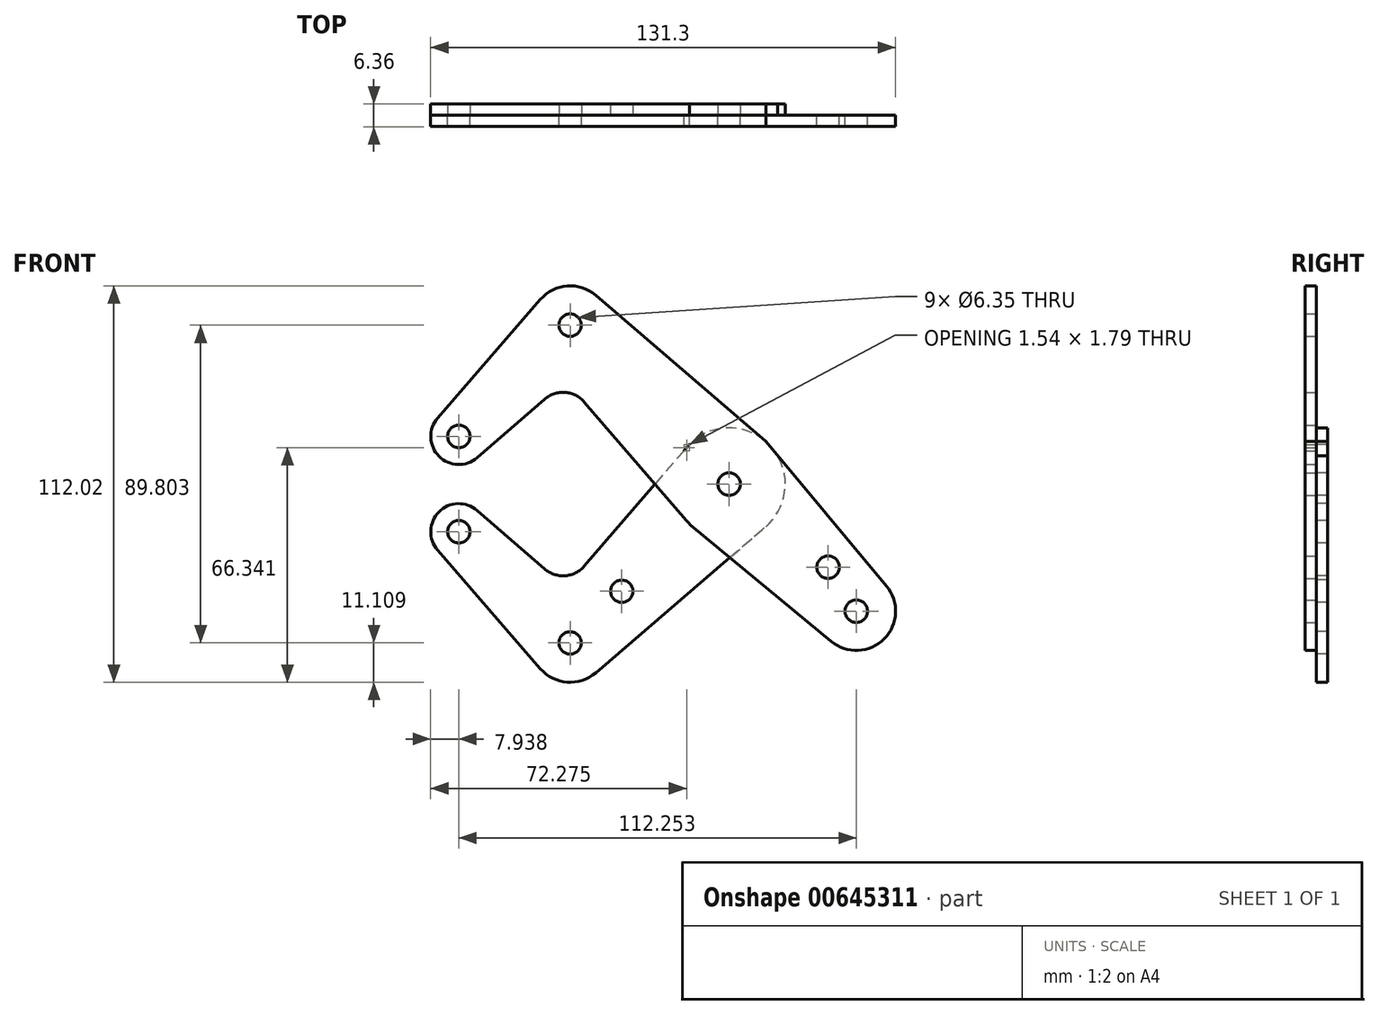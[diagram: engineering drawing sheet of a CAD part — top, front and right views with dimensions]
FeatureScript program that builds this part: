
annotation { "Feature Type Name" : "Feature", "Feature Type Description" : "" }
export const myFeature = defineFeature(function(context is Context, id is Id, definition is map)
    precondition{}
    {
        {
            var Q0;
            Q0=qCreatedBy(makeId("Front.planeOp"),FACE);
            var sketch = newSketch(context, id + "F0", { "sketchPlane" : qUnion([Q0])});
            skLineSegment(sketch, "E0", {"start": v(-76.33, 13.47) * mm, "end": v(-44.9, 44.9) * mm, "construction": true});
            skLineSegment(sketch, "E1", {"start": v(-44.9, 44.9) * mm, "end": v(35.92, -35.92) * mm, "construction": true});
            skCircle(sketch, "E2", {"center": v(-76.33, 13.47) * mm, "radius": 3.18 * mm});
            skCircle(sketch, "E3", {"center": v(-76.33, 13.47) * mm, "radius": 7.94 * mm});
            skCircle(sketch, "E4", {"center": v(-44.9, 44.9) * mm, "radius": 11.11 * mm});
            skCircle(sketch, "E5", {"center": v(-44.9, 44.9) * mm, "radius": 3.18 * mm});
            skCircle(sketch, "E6", {"center": v(0, 0) * mm, "radius": 15.88 * mm});
            skCircle(sketch, "E7", {"center": v(0, 0) * mm, "radius": 3.98 * mm});
            skCircle(sketch, "E8", {"center": v(0, 0) * mm, "radius": 3.18 * mm});
            skCircle(sketch, "E9", {"center": v(35.92, -35.92) * mm, "radius": 11.11 * mm});
            skCircle(sketch, "E10", {"center": v(35.92, -35.92) * mm, "radius": 3.18 * mm});
            skCircle(sketch, "E11", {"center": v(27.97, -23.48) * mm, "radius": 3.17 * mm});
            skLineSegment(sketch, "E12", {"start": v(-82.33, 18.67) * mm, "end": v(-53.3, 52.18) * mm});
            skLineSegment(sketch, "E13", {"start": v(-71.13, 7.47) * mm, "end": v(-52.08, 23.98) * mm});
            skLineSegment(sketch, "E14", {"start": v(-37.66, 53.33) * mm, "end": v(10.35, 12.04) * mm});
            skLineSegment(sketch, "E15", {"start": v(-10.12, -12.23) * mm, "end": v(28.83, -44.48) * mm});
            skLineSegment(sketch, "E16", {"start": v(10.35, 12.04) * mm, "end": v(44.45, -28.8) * mm});
            skArc(sketch, "E17.filletArc", {"start": v(-40.85, 23.15) * mm, "mid": v(-46.3, 25.9) * mm, "end": v(-52.08, 23.98) * mm});
            skLineSegment(sketch, "E18", {"start": v(0, 0) * mm, "end": v(-44.9, -44.9) * mm, "construction": true});
            skLineSegment(sketch, "E19", {"start": v(-44.9, -44.9) * mm, "end": v(-76.33, -13.47) * mm, "construction": true});
            skCircle(sketch, "E20", {"center": v(-76.33, -13.47) * mm, "radius": 7.94 * mm});
            skCircle(sketch, "E21", {"center": v(-76.33, -13.47) * mm, "radius": 3.18 * mm});
            skCircle(sketch, "E22", {"center": v(-44.9, -44.9) * mm, "radius": 11.11 * mm});
            skCircle(sketch, "E23", {"center": v(-44.9, -44.9) * mm, "radius": 3.18 * mm});
            skCircle(sketch, "E24", {"center": v(-30.3, -30.3) * mm, "radius": 3.18 * mm});
            skLineSegment(sketch, "E25", {"start": v(-11.23, 11.23) * mm, "end": v(-40.84, -23.16) * mm});
            skLineSegment(sketch, "E26", {"start": v(-37.66, -53.33) * mm, "end": v(11.26, -11.26) * mm});
            skLineSegment(sketch, "E27", {"start": v(-82.33, -18.67) * mm, "end": v(-53.3, -52.18) * mm});
            skLineSegment(sketch, "E28", {"start": v(-71.13, -7.47) * mm, "end": v(-52.07, -23.98) * mm});
            skArc(sketch, "E29.filletArc", {"start": v(-52.07, -23.98) * mm, "mid": v(-46.29, -25.9) * mm, "end": v(-40.84, -23.16) * mm});
            skLineSegment(sketch, "E30", {"start": v(-40.85, 23.15) * mm, "end": v(-12.04, -10.35) * mm});
            skSolve(sketch);
        }
        {
            var Q0;
            Q0=makeQuery(id+"F0.imprint","IMPRINT",FACE,{"disambiguationData":[TD([[makeQuery(id+"F0.imprint","IMPRINT",EDGE,{"derivedFrom":sQuery(id+"F0.wireOp",EDGE,"E2")}),-1.0]])]});
            var Q1;
            Q1=makeQuery(id+"F0.imprint","IMPRINT",FACE,{"disambiguationData":[TD([[makeQuery(id+"F0.imprint","IMPRINT",EDGE,{"derivedFrom":sQuery(id+"F0.wireOp",EDGE,"E5")}),-1.0]])]});
            var Q2;
            {var subQ5=sQuery(id+"F0.wireOp",EDGE,"E12");Q2=makeQuery(id+"F0.imprint","IMPRINT",FACE,{"disambiguationData":[TD([[makeQuery(id+"F0.imprint","IMPRINT",EDGE,{"derivedFrom":subQ5}),-1.0]])]});}
            var Q3;
            {var subQ0=sQuery(id+"F0.wireOp",EDGE,"MmRiEuoZ-qYsz-kD5B-3HoX-GEw2XtJWGpv0");var subQ3=sQuery(id+"F0.wireOp",EDGE,"E25");var subQ5=makeQuery(id+"F0.imprint","INTERSECT",VERTEX,{"derivedFrom":[subQ0,subQ3]});Q3=makeQuery(id+"F0.imprint","IMPRINT",FACE,{"disambiguationData":[TD([[makeQuery(id+"F0.imprint","IMPRINT",EDGE,{"disambiguationData":[TD([[subQ5,1.0]])],"derivedFrom":subQ3}),1.0]])]});}
            var Q4;
            Q4=makeQuery(id+"F0.imprint","IMPRINT",FACE,{"disambiguationData":[TD([[makeQuery(id+"F0.imprint","IMPRINT",EDGE,{"derivedFrom":sQuery(id+"F0.wireOp",EDGE,"E7")}),-1.0]])]});
            var Q5;
            Q5=makeQuery(id+"F0.imprint","IMPRINT",FACE,{"disambiguationData":[TD([[makeQuery(id+"F0.imprint","IMPRINT",EDGE,{"derivedFrom":sQuery(id+"F0.wireOp",EDGE,"E7")}),1.0]])]});
            var Q6;
            {var subQ1=sQuery(id+"F0.wireOp",EDGE,"E6");var subQ3=sQuery(id+"F0.wireOp",EDGE,"E26");var subQ4=makeQuery(id+"F0.imprint","INTERSECT",VERTEX,{"derivedFrom":[subQ1,subQ3]});Q6=makeQuery(id+"F0.imprint","IMPRINT",FACE,{"disambiguationData":[TD([[makeQuery(id+"F0.imprint","IMPRINT",EDGE,{"disambiguationData":[TD([[subQ4,1.0]])],"derivedFrom":subQ3}),1.0]])]});}
            var Q7;
            Q7=makeQuery(id+"F0.imprint","IMPRINT",FACE,{"disambiguationData":[TD([[makeQuery(id+"F0.imprint","IMPRINT",EDGE,{"derivedFrom":sQuery(id+"F0.wireOp",EDGE,"E11")}),-1.0]])]});
            var Q8;
            Q8=makeQuery(id+"F0.imprint","IMPRINT",FACE,{"disambiguationData":[TD([[makeQuery(id+"F0.imprint","IMPRINT",EDGE,{"derivedFrom":sQuery(id+"F0.wireOp",EDGE,"E10")}),-1.0]])]});
            extrude(context, id + "F1", {"entities" : qUnion([Q0, Q1, Q2, Q3, Q4, Q5, Q6, Q7, Q8]), "depth" : 3.17 * mm, "offsetDistance" : 25.4 * mm});
        }
        {
            var Q0;
            Q0=makeQuery(id+"F0.imprint","IMPRINT",FACE,{"disambiguationData":[TD([[makeQuery(id+"F0.imprint","IMPRINT",EDGE,{"derivedFrom":sQuery(id+"F0.wireOp",EDGE,"E21")}),-1.0]])]});
            var Q1;
            Q1=makeQuery(id+"F0.imprint","IMPRINT",FACE,{"disambiguationData":[TD([[makeQuery(id+"F0.imprint","IMPRINT",EDGE,{"derivedFrom":sQuery(id+"F0.wireOp",EDGE,"E24")}),-1.0]])]});
            var Q2;
            Q2=makeQuery(id+"F0.imprint","IMPRINT",FACE,{"disambiguationData":[TD([[makeQuery(id+"F0.imprint","IMPRINT",EDGE,{"derivedFrom":sQuery(id+"F0.wireOp",EDGE,"E23")}),-1.0]])]});
            var Q3;
            {var subQ0=sQuery(id+"F0.wireOp",EDGE,"E15");var subQ1=sQuery(id+"F0.wireOp",EDGE,"E6");var subQ2=makeQuery(id+"F0.imprint","INTERSECT",VERTEX,{"derivedFrom":[subQ1,subQ0]});Q3=makeQuery(id+"F0.imprint","IMPRINT",FACE,{"disambiguationData":[TD([[makeQuery(id+"F0.imprint","IMPRINT",EDGE,{"disambiguationData":[TD([[subQ2,-1.0]])],"derivedFrom":subQ1}),-1.0]])]});}
            var Q4;
            {var subQ0=sQuery(id+"F0.wireOp",EDGE,"E30");var subQ1=sQuery(id+"F0.wireOp",EDGE,"E6");var subQ2=makeQuery(id+"F0.imprint","INTERSECT",VERTEX,{"derivedFrom":[subQ1,subQ0]});Q4=makeQuery(id+"F0.imprint","IMPRINT",FACE,{"disambiguationData":[TD([[makeQuery(id+"F0.imprint","IMPRINT",EDGE,{"disambiguationData":[TD([[subQ2,1.0]])],"derivedFrom":subQ1}),-1.0]])]});}
            var Q5;
            Q5=makeQuery(id+"F0.imprint","IMPRINT",FACE,{"disambiguationData":[TD([[makeQuery(id+"F0.imprint","IMPRINT",EDGE,{"derivedFrom":sQuery(id+"F0.wireOp",EDGE,"E7")}),-1.0]])]});
            var Q6;
            Q6=makeQuery(id+"F0.imprint","IMPRINT",FACE,{"disambiguationData":[TD([[makeQuery(id+"F0.imprint","IMPRINT",EDGE,{"derivedFrom":sQuery(id+"F0.wireOp",EDGE,"E7")}),1.0]])]});
            extrude(context, id + "F2", {"entities" : qUnion([Q0, Q1, Q2, Q3, Q4, Q5, Q6]), "oppositeDirection" : true, "depth" : 3.17 * mm, "offsetDistance" : 25.4 * mm});
        }
    });
